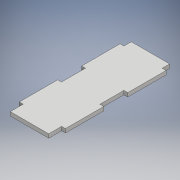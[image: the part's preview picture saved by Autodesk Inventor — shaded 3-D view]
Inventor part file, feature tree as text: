
AUTODESK INVENTOR PART (.ipt)
format: ipt  version: 2018 (Build 220112000, 112)  size: 112,640 bytes
history: native  units: mm
features: extrude x1, sketch x1
ambient origin geometry x8: Origin, YZ Plane, XZ Plane, XY Plane, X Axis, Y Axis, Z Axis, Center Point
bodies: Solid1 (feature_tree)
feature tree (2):
  extrude  "Extrusion1"  Depth=40.0mm
  sketch  "Sketch1"  dims[d0=4.0mm d1=40.0mm d2=40.0mm d3=40.0mm d4=4.0mm d5=0.0mm]
